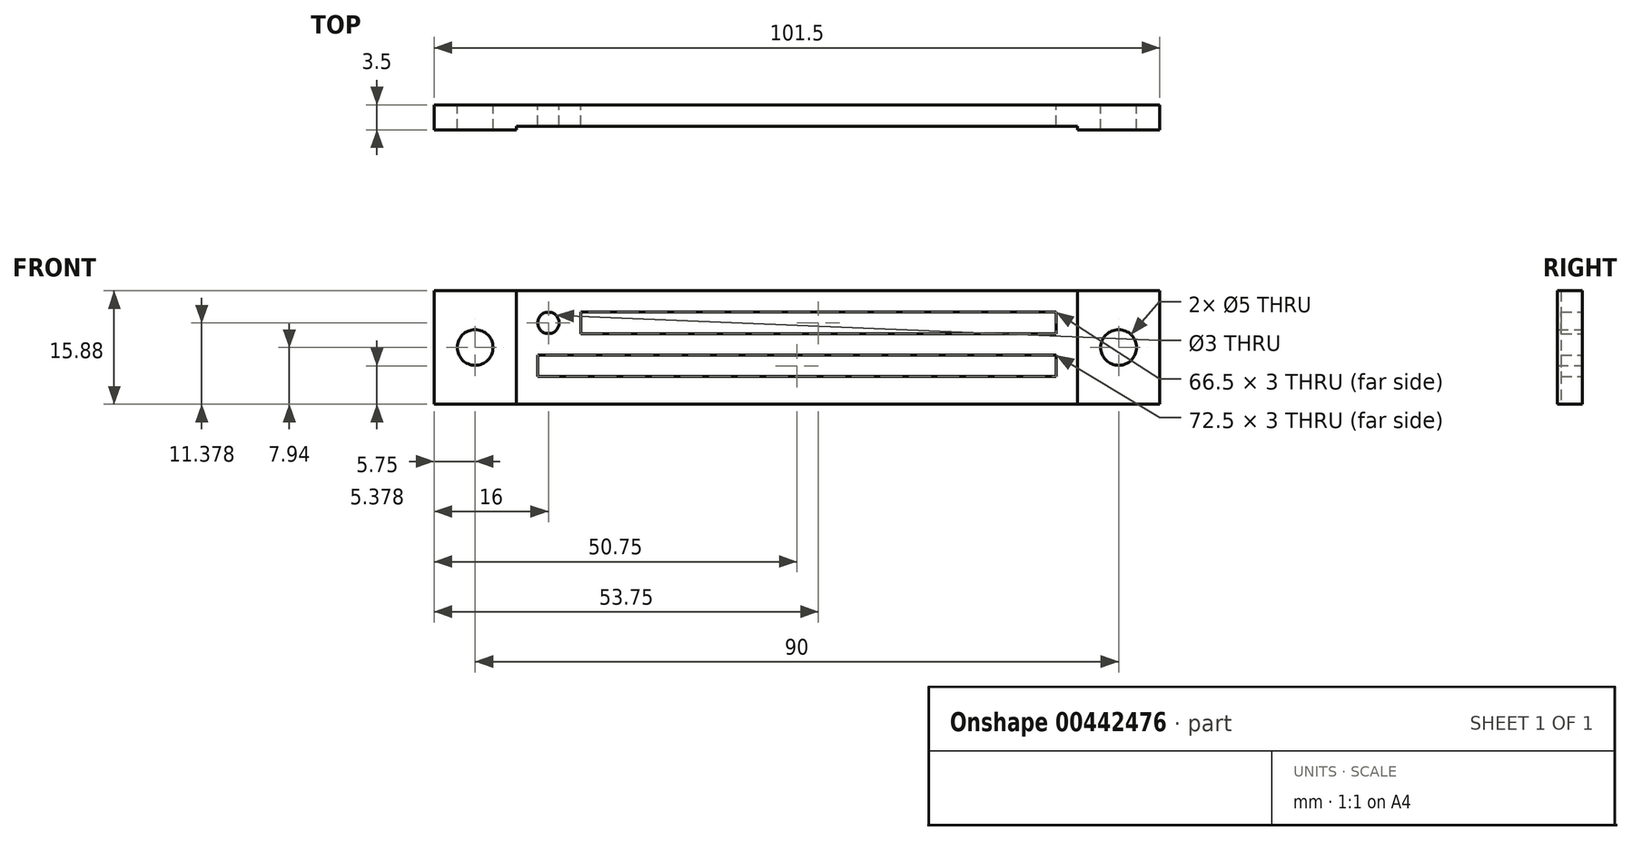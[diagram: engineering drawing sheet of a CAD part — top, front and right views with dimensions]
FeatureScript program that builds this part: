
annotation { "Feature Type Name" : "Feature", "Feature Type Description" : "" }
export const myFeature = defineFeature(function(context is Context, id is Id, definition is map)
    precondition{}
    {
        {
            var Q0;
            Q0=qCreatedBy(makeId("Front.planeOp"),FACE);
            var sketch = newSketch(context, id + "F0", { "sketchPlane" : qUnion([Q0])});
            skLineSegment(sketch, "E0.bottom", {"start": v(50.75, 7.94) * mm, "end": v(-50.75, 7.94) * mm});
            skLineSegment(sketch, "E0.top", {"start": v(50.75, -7.94) * mm, "end": v(-50.75, -7.94) * mm});
            skLineSegment(sketch, "E0.left", {"start": v(50.75, 7.94) * mm, "end": v(50.75, -7.94) * mm});
            skLineSegment(sketch, "E0.right", {"start": v(-50.75, 7.94) * mm, "end": v(-50.75, -7.94) * mm});
            skPoint(sketch, "E0.middle", {"position": v(0, 0) * mm});
            skLineSegment(sketch, "E1.bottom", {"start": v(39.25, 7.94) * mm, "end": v(-39.25, 7.94) * mm, "construction": true});
            skLineSegment(sketch, "E1.top", {"start": v(39.25, -7.94) * mm, "end": v(-39.25, -7.94) * mm, "construction": true});
            skLineSegment(sketch, "E1.left", {"start": v(39.25, 7.94) * mm, "end": v(39.25, -7.94) * mm, "construction": true});
            skLineSegment(sketch, "E1.right", {"start": v(-39.25, 7.94) * mm, "end": v(-39.25, -7.94) * mm, "construction": true});
            skLineSegment(sketch, "E2", {"start": v(-50.75, 7.94) * mm, "end": v(-39.25, -7.94) * mm, "construction": true});
            skLineSegment(sketch, "E3", {"start": v(39.25, -7.94) * mm, "end": v(50.75, 7.94) * mm, "construction": true});
            skCircle(sketch, "E4", {"center": v(45, 0) * mm, "radius": 2.5 * mm});
            skCircle(sketch, "E5", {"center": v(-45, 0) * mm, "radius": 2.5 * mm});
            skCircle(sketch, "E6", {"center": v(-34.75, 3.44) * mm, "radius": 1.5 * mm});
            skLineSegment(sketch, "E7.bottom", {"start": v(-30.25, 4.94) * mm, "end": v(36.25, 4.94) * mm});
            skLineSegment(sketch, "E7.top", {"start": v(-30.25, 1.94) * mm, "end": v(36.25, 1.94) * mm});
            skLineSegment(sketch, "E7.left", {"start": v(-30.25, 4.94) * mm, "end": v(-30.25, 1.94) * mm});
            skLineSegment(sketch, "E7.right", {"start": v(36.25, 4.94) * mm, "end": v(36.25, 1.94) * mm});
            skLineSegment(sketch, "E8.bottom", {"start": v(-36.25, -1.06) * mm, "end": v(36.25, -1.06) * mm});
            skLineSegment(sketch, "E8.top", {"start": v(-36.25, -4.06) * mm, "end": v(36.25, -4.06) * mm});
            skLineSegment(sketch, "E8.left", {"start": v(-36.25, -1.06) * mm, "end": v(-36.25, -4.06) * mm});
            skLineSegment(sketch, "E8.right", {"start": v(36.25, -1.06) * mm, "end": v(36.25, -4.06) * mm});
            skSolve(sketch);
        }
        {
            var Q0;
            Q0 = qSketchRegion(id + "F0", true);
            extrude(context, id + "F1", {"entities" : qUnion([Q0]), "depth" : 3.5 * mm});
        }
        {
            var Q0;
            Q0=makeQuery(id+"F1.opExtrude","CAP_FACE",FACE,{"disambiguationData":[OSD([sQuery(id+"F0.wireOp",EDGE,"E0.bottom"),sQuery(id+"F0.wireOp",EDGE,"E0.top"),sQuery(id+"F0.wireOp",EDGE,"E0.left"),sQuery(id+"F0.wireOp",EDGE,"E0.right"),sQuery(id+"F0.wireOp",EDGE,"E4"),sQuery(id+"F0.wireOp",EDGE,"E5"),sQuery(id+"F0.wireOp",EDGE,"E6"),sQuery(id+"F0.wireOp",EDGE,"E7.bottom"),sQuery(id+"F0.wireOp",EDGE,"E7.top"),sQuery(id+"F0.wireOp",EDGE,"E7.left"),sQuery(id+"F0.wireOp",EDGE,"E7.right"),sQuery(id+"F0.wireOp",EDGE,"E8.bottom"),sQuery(id+"F0.wireOp",EDGE,"E8.top"),sQuery(id+"F0.wireOp",EDGE,"E8.left"),sQuery(id+"F0.wireOp",EDGE,"E8.right")])],"isStart":false});
            var sketch = newSketch(context, id + "F2", { "sketchPlane" : qUnion([Q0])});
            skLineSegment(sketch, "E9.bottom", {"start": v(39.25, 7.94) * mm, "end": v(-39.25, 7.94) * mm});
            skLineSegment(sketch, "E9.top", {"start": v(39.25, -7.94) * mm, "end": v(-39.25, -7.94) * mm});
            skLineSegment(sketch, "E9.left", {"start": v(39.25, 7.94) * mm, "end": v(39.25, -7.94) * mm});
            skLineSegment(sketch, "E9.right", {"start": v(-39.25, 7.94) * mm, "end": v(-39.25, -7.94) * mm});
            skPoint(sketch, "E9.middle", {"position": v(0, 0) * mm});
            skSolve(sketch);
        }
        {
            var Q0;
            Q0 = qSketchRegion(id + "F2", true);
            extrude(context, id + "F3", {"entities" : qUnion([Q0]), "operationType" : NewBodyOperationType.REMOVE, "oppositeDirection" : true, "depth" : .5 * mm});
        }
    });
